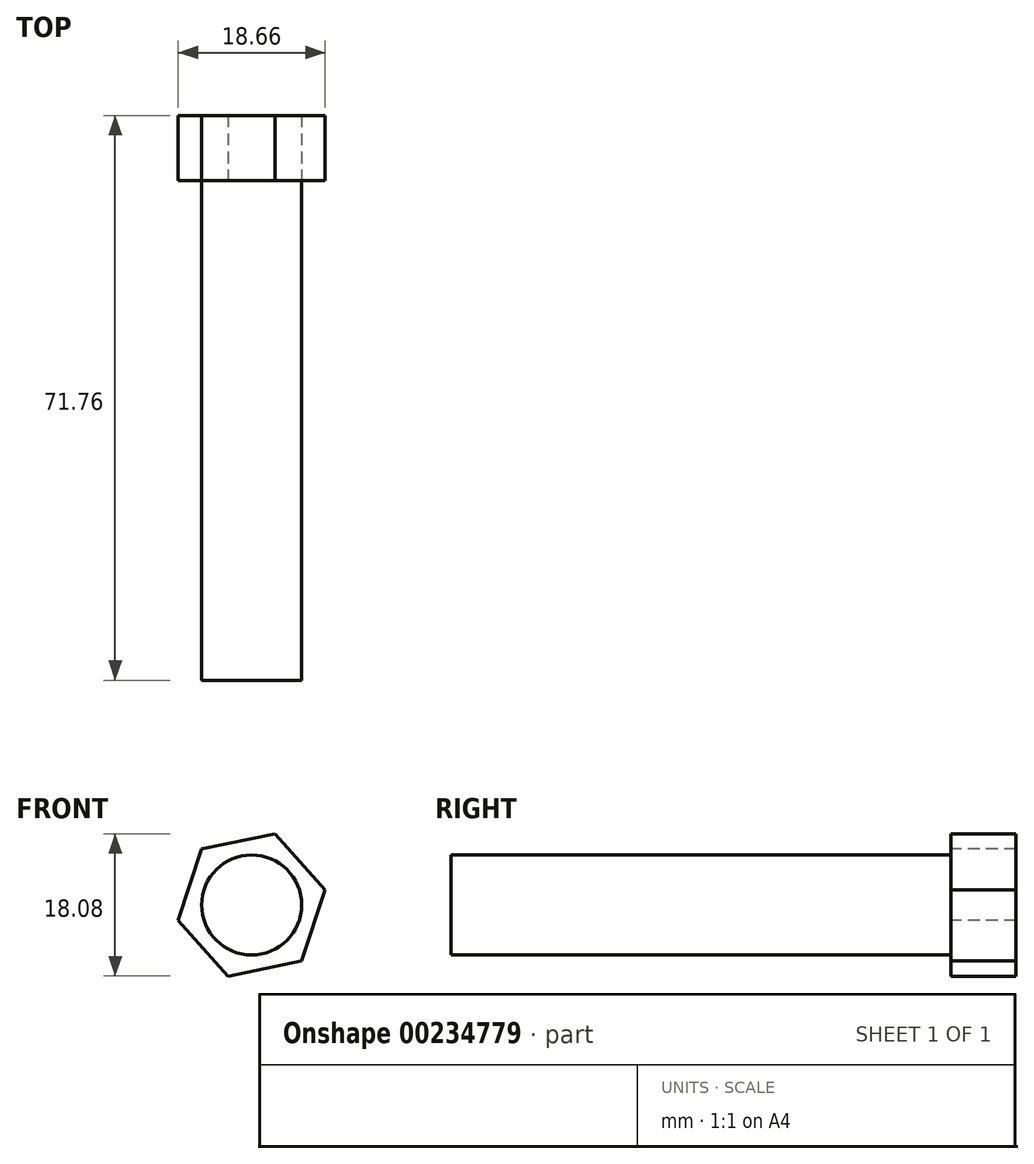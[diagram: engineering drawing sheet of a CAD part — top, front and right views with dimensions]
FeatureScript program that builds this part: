
annotation { "Feature Type Name" : "Feature", "Feature Type Description" : "" }
export const myFeature = defineFeature(function(context is Context, id is Id, definition is map)
    precondition{}
    {
        {
            var Q0;
            Q0=qCreatedBy(makeId("Front.planeOp"),FACE);
            var sketch = newSketch(context, id + "F2", { "sketchPlane" : qUnion([Q0])});
            skCircle(sketch, "E0", {"center": v(0, 0) * mm, "radius": 6.35 * mm});
            skCircle(sketch, "E1.cCircle", {"center": v(0, 0) * mm, "radius": 9.53 * mm, "construction": true});
            skLineSegment(sketch, "E1.0", {"start": v(6.33, -7.11) * mm, "end": v(-3, -9.04) * mm});
            skLineSegment(sketch, "E1.1", {"start": v(-3, -9.04) * mm, "end": v(-9.33, -1.93) * mm});
            skLineSegment(sketch, "E1.2", {"start": v(-9.33, -1.93) * mm, "end": v(-6.33, 7.11) * mm});
            skLineSegment(sketch, "E1.3", {"start": v(-6.33, 7.11) * mm, "end": v(3, 9.04) * mm});
            skLineSegment(sketch, "E1.4", {"start": v(3, 9.04) * mm, "end": v(9.33, 1.93) * mm});
            skLineSegment(sketch, "E1.5", {"start": v(9.33, 1.93) * mm, "end": v(6.33, -7.11) * mm});
            skSolve(sketch);
        }
        {
            var Q0;
            Q0=makeQuery(id+"F2.imprint","IMPRINT",FACE,{"disambiguationData":[TD([[makeQuery(id+"F2.imprint","IMPRINT",EDGE,{"derivedFrom":sQuery(id+"F2.wireOp",EDGE,"E0")}),1.0]])]});
            extrude(context, id + "F0", {"entities" : qUnion([Q0]), "depth" : 63.5 * mm});
        }
        {
            var Q0;
            Q0=makeQuery(id+"F2.imprint","IMPRINT",FACE,{"disambiguationData":[TD([[makeQuery(id+"F2.imprint","IMPRINT",EDGE,{"derivedFrom":sQuery(id+"F2.wireOp",EDGE,"E0")}),-1.0]])]});
            var Q1;
            Q1=makeQuery(id+"F2.imprint","IMPRINT",FACE,{"disambiguationData":[TD([[makeQuery(id+"F2.imprint","IMPRINT",EDGE,{"derivedFrom":sQuery(id+"F2.wireOp",EDGE,"E0")}),1.0]])]});
            extrude(context, id + "F1", {"entities" : qUnion([Q0, Q1]), "operationType" : NewBodyOperationType.ADD, "oppositeDirection" : true, "depth" : 8.25 * mm});
        }
    });
